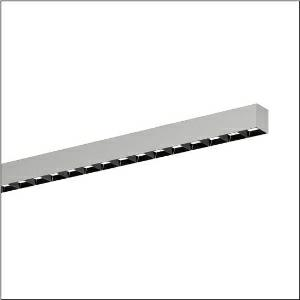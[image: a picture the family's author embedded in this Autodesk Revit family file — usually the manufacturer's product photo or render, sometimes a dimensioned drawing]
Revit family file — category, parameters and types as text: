
# Revit family: silica_21_51mx24dc4asb
name_source: partatom
category: Lighting Fixtures
units: mm (PartAtom-declared; Revit-internal decimal feet)

## family parameters
Cut with Voids When Loaded = No
Host = Face
Light Source = No
Part Type = Normal
Room Calculation Point = No
Round Connector Dimension = Use Diameter
Shared = No

## types (1)
- --- (1 x LED, 10800 lm, 73.7 W, 4000K)
    Apparent Load = 74 VA
    CIE Flux Codes = 74 94 99 100 100
    Color Rendering = 80
    Color Temperature = 4000K
    Default Elevation = 1800 mm
    Description = Silica 21, office luminaire, primary light control with darklight reflector, of PMMA, black, CAT 2 (L<= 3000cd/m²), light emission: direct distribution, primary light characteristic: asymmetric, installation type: surface-mounted, LED, rated luminous flux: 10.800lm, luminous efficacy: 147lm/W, light colour: 840, colour temperature: 4000K, control gear: DALI 2, with terminal, 3+2-pole, max. 2.5mm², mains connection: 220..240V, AC, 50/60Hz, rated input power: 73.7W, luminaire housing, of aluminium, metallic grey (RAL 9006), length: 3.004mm, width: 53mm, height: 53mm, protection rating (complete): IP20, insulation class (complete): insulation class I (protective earthing), certification: CE, permissible operating ambient temperature: 0..+35°C, standard: EN 50419, packaging unit: 1 piece
    Height = 53 mm
    Lamp = 1 x LED
    Lamp Light Flux = 10800 lm
    Lamp Power = 73.7 W
    Lamp count = 1
    Length = 3004 mm
    Luminous efficacy = 147 lm/W
    Manufacturer = Siteco
    ModVariant = No
    Model = 51MX24DC4ASB
    Mounting Place = Ceiling
    Mounting Type = Surface mounted
    Number of Poles = 1
    OnlyDefault = Yes
    Power Factor = 1
    Product Name = Silica 21
    Product group = office luminaire | ceiling mounted
    ProductGroupID = 301
    Protection Class = Protection class I
    Protection Degree = IP 20
    RLX_Detail_Level = 1
    RLX_Emergency_Light_Flux = 0 lm
    RLX_Emergency_Type = 0
    RLX_Emergency_Type_DB = No
    RlxData = <blob elided: 63905 chars, md5=5e582dbb>
    Socket = socket
    Standby Power = 0 W
    System Light Flux = 10800 lm
    System Power = 74 W
    Type Comments = factory setting: luminous flux: 100 % | dim-lin: 254 | 418 mA
    Type Image = l_1335929.jpg
    URL = http://relux.com
    VarID = @adj_122781
    Voltage = 0 V
    Weight = 0.00 kg
    Width = 53 mm

## geometry (parser evidence)
native form markers: Blend x4, Sweep x10
no freeform markers — native parametric forms only
